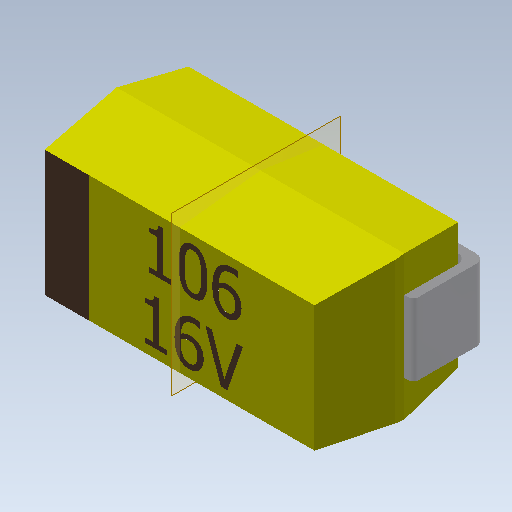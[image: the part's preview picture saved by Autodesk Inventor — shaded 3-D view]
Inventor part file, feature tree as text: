
AUTODESK INVENTOR PART (.ipt)
format: ipt  version: 2020.3 (Build 243373000, 373)  size: 373,248 bytes
history: native  units: mm
features: chamfer x8, extrude x5, sketch x5, fillet x2, plane x1, mirror x1, projected_geometry x1
ambient origin geometry x8: Origin, YZ Plane, XZ Plane, XY Plane, X Axis, Y Axis, Z Axis, Center Point
bodies: Solid1 (feature_tree)
feature tree (23):
  extrude  "Extrusion1"  Depth=3.2mm
  chamfer  "Chamfer2"  Distance=1.6mm
  chamfer  "Chamfer3"  Distance=0.9mm Angle=45.0deg
  chamfer  "Chamfer4"  Distance=0.9mm Angle=45.0deg
  chamfer  "Chamfer5"  Distance=0.9mm Angle=45.0deg
  chamfer  "Chamfer6"  Distance=0.7mm Angle=45.0deg
  chamfer  "Chamfer7"  Distance=0.7mm Angle=45.0deg
  chamfer  "Chamfer8"  Distance=0.7mm Angle=45.0deg
  extrude  "Extrusion2"  Depth=0.8mm
  extrude  "Extrusion3"  Depth=0.1mm
  plane  "Work Plane1"
  mirror  "Mirror1"
  fillet  "Fillet1"  Radius=0.1mm
  fillet  "Fillet2"  Radius=0.1mm
  chamfer  "Chamfer9"  Distance=0.8mm
  extrude  "Extrusion4"  Depth=0.05mm
  extrude  "Extrusion5"  Depth=0.8mm TaperAngle=45.0deg
  sketch  "Sketch1"  dims[d0=1.6mm d1=3.2mm d2=1.6mm d3=0.0mm d7=0.9mm d8=0.1mm d9=45.0deg d10=0.9mm d11=0.1mm d12=45.0deg d13=0.9mm d14=0.1mm d15=45.0deg d16=0.7mm d17=0.1mm d18=45.0deg d19=0.7mm d20=0.1mm d21=45.0deg d22=0.7mm d23=0.1mm d24=45.0deg]
  sketch  "Sketch2"  dims[d25=0.7mm d26=0.1mm d27=45.0deg d28=0.8mm]
  projected_geometry  "Projected Loop1"
  sketch  "Sketch3"  dims[d29=0.4mm d30=0.1mm d31=0.1mm d32=0.0mm d33=0.1mm d34=0.8mm d35=0.0mm]
  sketch  "Sketch4"  dims[d36=1.6mm d37=0.05mm]
  sketch  "Sketch5"  dims[d38=0.1mm d39=0.8mm d40=0.1mm d41=45.0deg d42=0.001mm d43=0.0mm d44=0.001mm d45=0.0mm]
